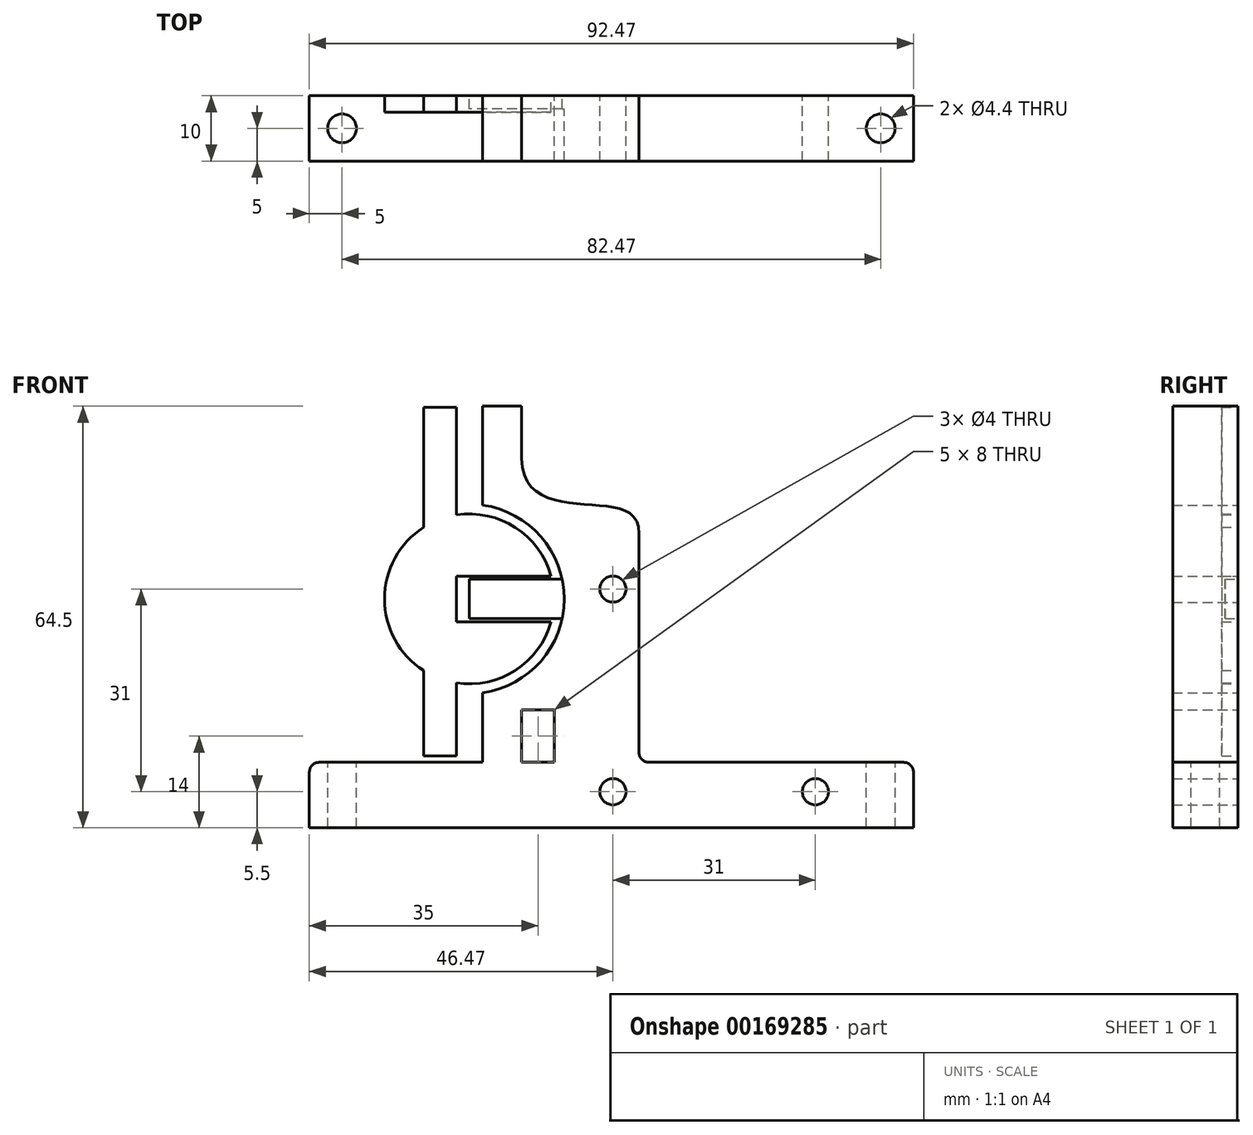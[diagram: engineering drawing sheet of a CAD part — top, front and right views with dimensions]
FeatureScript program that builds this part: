
annotation { "Feature Type Name" : "Feature", "Feature Type Description" : "" }
export const myFeature = defineFeature(function(context is Context, id is Id, definition is map)
    precondition{}
    {
        {
            var Q0;
            Q0=qCreatedBy(makeId("Front.planeOp"),FACE);
            var sketch = newSketch(context, id + "F0", { "sketchPlane" : qUnion([Q0])});
            skLineSegment(sketch, "E0.bottom", {"start": v(0, 0) * mm, "end": v(52, 0) * mm});
            skLineSegment(sketch, "E0.top", {"start": v(0, 10) * mm, "end": v(52, 10) * mm});
            skLineSegment(sketch, "E0.right", {"start": v(52, 0) * mm, "end": v(52, 10) * mm});
            skPoint(sketch, "E1", {"position": v(6, 5.5) * mm});
            skPoint(sketch, "E2", {"position": v(37, 5.5) * mm});
            skLineSegment(sketch, "E3", {"start": v(0, 0) * mm, "end": v(0, 45) * mm, "construction": true});
            skLineSegment(sketch, "E4", {"start": v(0, 45) * mm, "end": v(10, 45) * mm, "construction": true});
            skLineSegment(sketch, "E5", {"start": v(10, 45) * mm, "end": v(10, 10) * mm});
            skLineSegment(sketch, "E6", {"start": v(6, 0) * mm, "end": v(6, 45) * mm, "construction": true});
            skPoint(sketch, "E7", {"position": v(6, 36.5) * mm});
            skLineSegment(sketch, "E8", {"start": v(0, 5.5) * mm, "end": v(52, 5.5) * mm, "construction": true});
            skCircle(sketch, "E9", {"center": v(21.5, 21) * mm, "radius": 21.92 * mm, "construction": true});
            skCircle(sketch, "E10", {"center": v(21.5, 21) * mm, "radius": 10 * mm, "construction": true});
            skCircle(sketch, "E11", {"center": v(21.5, 21) * mm, "radius": 40 * mm, "construction": true});
            skPoint(sketch, "E12", {"position": v(-15.97, 35) * mm});
            skCircle(sketch, "E13", {"center": v(-15.97, 35) * mm, "radius": 11 * mm, "construction": true});
            skCircle(sketch, "E14", {"center": v(-15.97, 35) * mm, "radius": 7.5 * mm, "construction": true});
            skCircle(sketch, "E15", {"center": v(-15.97, 35) * mm, "radius": 14.5 * mm});
            skLineSegment(sketch, "E16", {"start": v(-30.47, 35) * mm, "end": v(-30.47, 0) * mm, "construction": true});
            skLineSegment(sketch, "E17", {"start": v(0, 0) * mm, "end": v(-30.47, 0) * mm});
            skLineSegment(sketch, "E18", {"start": v(-30.47, 0) * mm, "end": v(-40.47, 0) * mm});
            skLineSegment(sketch, "E19", {"start": v(-40.47, 0) * mm, "end": v(-40.47, 10) * mm});
            skLineSegment(sketch, "E20", {"start": v(-40.47, 10) * mm, "end": v(-30.47, 10) * mm});
            skLineSegment(sketch, "E21", {"start": v(21.5, 21) * mm, "end": v(-15.97, 35) * mm, "construction": true});
            skLineSegment(sketch, "E22", {"start": v(-15.97, 68.93) * mm, "end": v(-15.97, 10) * mm, "construction": true});
            skLineSegment(sketch, "E23", {"start": v(-30.47, 10) * mm, "end": v(0, 10) * mm});
            skLineSegment(sketch, "E24", {"start": v(-13.97, 10) * mm, "end": v(-13.97, 64.5) * mm});
            skLineSegment(sketch, "E25", {"start": v(-13.97, 64.5) * mm, "end": v(-7.97, 64.5) * mm});
            skLineSegment(sketch, "E26", {"start": v(-15.97, 38) * mm, "end": v(-15.97, 32) * mm});
            skLineSegment(sketch, "E27", {"start": v(-15.97, 32) * mm, "end": v(0, 32) * mm});
            skLineSegment(sketch, "E28", {"start": v(0, 32) * mm, "end": v(0, 38) * mm});
            skLineSegment(sketch, "E29", {"start": v(0, 38) * mm, "end": v(-15.97, 38) * mm});
            skLineSegment(sketch, "E30", {"start": v(-7.97, 64.5) * mm, "end": v(-7.97, 56.5) * mm});
            skFitSpline(sketch, "E31", {"points": [v(-7.97, 56.5) * mm, v(2.03, 49.43) * mm, v(10, 45) * mm], "startDerivative": vector(0.3, -33.73) * mm, "endDerivative": vector(-0.3, -26.17) * mm});
            skLineSegment(sketch, "E32", {"start": v(-7.97, 10) * mm, "end": v(-7.97, 18) * mm});
            skLineSegment(sketch, "E33", {"start": v(-7.97, 18) * mm, "end": v(-2.97, 18) * mm});
            skLineSegment(sketch, "E34", {"start": v(-2.97, 18) * mm, "end": v(-2.97, 10) * mm});
            skSolve(sketch);
        }
        {
            var Q0;
            {var subQ5=sQuery(id+"F0.wireOp",EDGE,"E0.bottom");Q0=makeQuery(id+"F0.imprint","IMPRINT",FACE,{"disambiguationData":[TD([[makeQuery(id+"F0.imprint","IMPRINT",EDGE,{"derivedFrom":subQ5}),1.0]])]});}
            var Q1;
            {var subQ4=sQuery(id+"F0.wireOp",EDGE,"E4");Q1=makeQuery(id+"F0.imprint","IMPRINT",FACE,{"disambiguationData":[TD([[makeQuery(id+"F0.imprint","IMPRINT",EDGE,{"derivedFrom":subQ4}),-1.0]])]});}
            var Q2;
            {var subQ7=sQuery(id+"F0.wireOp",EDGE,"E17");Q2=makeQuery(id+"F0.imprint","IMPRINT",FACE,{"disambiguationData":[TD([[makeQuery(id+"F0.imprint","IMPRINT",EDGE,{"derivedFrom":subQ7}),-1.0]])]});}
            var Q3;
            {var subQ0=sQuery(id+"F0.wireOp",EDGE,"E18");Q3=makeQuery(id+"F0.imprint","IMPRINT",FACE,{"disambiguationData":[TD([[makeQuery(id+"F0.imprint","IMPRINT",EDGE,{"derivedFrom":subQ0}),-1.0]])]});}
            var Q4;
            Q4=makeQuery(id+"F0.imprint","IMPRINT",FACE,{"disambiguationData":[TD([[makeQuery(id+"F0.imprint","IMPRINT",EDGE,{"derivedFrom":sQuery(id+"F0.wireOp",EDGE,"E4")}),1.0]])]});
            var Q5;
            {var subQ0=sQuery(id+"F0.wireOp",EDGE,"E25");Q5=makeQuery(id+"F0.imprint","IMPRINT",FACE,{"disambiguationData":[TD([[makeQuery(id+"F0.imprint","IMPRINT",EDGE,{"derivedFrom":subQ0}),-1.0]])]});}
            var Q6;
            {var subQ5=sQuery(id+"F0.wireOp",EDGE,"E28");Q6=makeQuery(id+"F0.imprint","IMPRINT",FACE,{"disambiguationData":[TD([[makeQuery(id+"F0.imprint","IMPRINT",EDGE,{"derivedFrom":subQ5}),1.0]])]});}
            var Q7;
            {var subQ0=sQuery(id+"F0.wireOp",EDGE,"E24");var subQ1=sQuery(id+"F0.wireOp",EDGE,"E15");var subQ2=makeQuery(id+"F0.imprint","INTERSECT",VERTEX,{"disambiguationData":[OD(1.0)],"derivedFrom":[subQ1,subQ0]});Q7=makeQuery(id+"F0.imprint","IMPRINT",FACE,{"disambiguationData":[TD([[makeQuery(id+"F0.imprint","IMPRINT",EDGE,{"disambiguationData":[TD([[subQ2,-1.0]])],"derivedFrom":subQ1}),-1.0]])]});}
            extrude(context, id + "F1", {"entities" : qUnion([Q0, Q1, Q2, Q3, Q4, Q5, Q6, Q7]), "depth" : 10 * mm});
        }
        {
            var Q0;
            Q0=sQuery(id+"F0.wireOp",VERTEX,"E7");
            var Q1;
            Q1=sQuery(id+"F0.wireOp",VERTEX,"E1");
            var Q2;
            Q2=sQuery(id+"F0.wireOp",VERTEX,"E2");
            var Q3;
            Q3=makeQuery(id+"F1.opExtrude","SWEPT_BODY",BODY,{"disambiguationData":[OSD([sQuery(id+"F0.wireOp",EDGE,"E0.bottom"),sQuery(id+"F0.wireOp",EDGE,"E0.top"),sQuery(id+"F0.wireOp",EDGE,"E0.right"),sQuery(id+"F0.wireOp",EDGE,"E4"),sQuery(id+"F0.wireOp",EDGE,"E5"),sQuery(id+"F0.wireOp",EDGE,"E15"),sQuery(id+"F0.wireOp",EDGE,"E17"),sQuery(id+"F0.wireOp",EDGE,"E18"),sQuery(id+"F0.wireOp",EDGE,"E19"),sQuery(id+"F0.wireOp",EDGE,"E20"),sQuery(id+"F0.wireOp",EDGE,"Px57lK6U-PPyR-QxDG-lkTx-4ku2XlHoAHPM"),sQuery(id+"F0.wireOp",EDGE,"9lGXsvYk-Ba66-BwJE-tG4q-ajGsNSx14eTR"),sQuery(id+"F0.wireOp",EDGE,"7AF7hhR4-0pg7-JyBW-10Vu-YeYs19Hmrawn"),sQuery(id+"F0.wireOp",EDGE,"SDQQGvJ1-Wn1U-Uzs4-qJnu-05INEi9zJf3w"),sQuery(id+"F0.wireOp",EDGE,"92fyXlvB-mwCe-QFS7-udCC-Qqv6sfzYrIQP"),sQuery(id+"F0.wireOp",EDGE,"BwISZ355-k5cW-KgOS-BZip-VC8WJniyM8gW")])]});
            hole(context, id + "F2", {"style" : HoleStyle.SIMPLE, "endStyle" : HoleEndStyle.THROUGH, "oppositeDirection" : true, "holeDiameter" : 4 * mm, "locations" : qUnion([Q0, Q1, Q2]), "scope" : qUnion([Q3]), "isTappedThrough" : true});
        }
        {
            var Q0;
            {var subQ0=sQuery(id+"F0.wireOp",EDGE,"E29");var subQ1=sQuery(id+"F0.wireOp",EDGE,"E15");var subQ2=makeQuery(id+"F0.imprint","INTERSECT",VERTEX,{"derivedFrom":[subQ1,subQ0]});Q0=makeQuery(id+"F0.imprint","IMPRINT",FACE,{"disambiguationData":[TD([[makeQuery(id+"F0.imprint","IMPRINT",EDGE,{"disambiguationData":[TD([[subQ2,1.0]])],"derivedFrom":subQ1}),1.0]])]});}
            var Q1;
            {var subQ5=sQuery(id+"F0.wireOp",EDGE,"E26");Q1=makeQuery(id+"F0.imprint","IMPRINT",FACE,{"disambiguationData":[TD([[makeQuery(id+"F0.imprint","IMPRINT",EDGE,{"derivedFrom":subQ5}),1.0]])]});}
            extrude(context, id + "F3", {"entities" : qUnion([Q0, Q1]), "operationType" : NewBodyOperationType.ADD, "depth" : 2 * mm});
        }
        {
            var Q0;
            Q0=qCreatedBy(makeId("Front.planeOp"),FACE);
            var sketch = newSketch(context, id + "F4", { "sketchPlane" : qUnion([Q0])});
            skCircle(sketch, "E35", {"center": v(-15.97, 35) * mm, "radius": 13 * mm});
            skLineSegment(sketch, "E36", {"start": v(-3.45, 38.5) * mm, "end": v(-17.97, 38.5) * mm});
            skLineSegment(sketch, "E37", {"start": v(-17.97, 38.5) * mm, "end": v(-17.97, 31.5) * mm});
            skLineSegment(sketch, "E38", {"start": v(-17.97, 31.5) * mm, "end": v(-3.45, 31.5) * mm});
            skLineSegment(sketch, "E39", {"start": v(-15.97, 35) * mm, "end": v(-15.97, 70.7) * mm, "construction": true});
            skLineSegment(sketch, "E40", {"start": v(-17.97, 47.85) * mm, "end": v(-17.97, 64.35) * mm});
            skLineSegment(sketch, "E41", {"start": v(-17.97, 64.35) * mm, "end": v(-22.97, 64.35) * mm});
            skLineSegment(sketch, "E42", {"start": v(-22.97, 64.35) * mm, "end": v(-22.97, 45.95) * mm});
            skLineSegment(sketch, "E43", {"start": v(-17.97, 22.15) * mm, "end": v(-17.97, 11) * mm});
            skLineSegment(sketch, "E44", {"start": v(-17.97, 11) * mm, "end": v(-22.97, 11) * mm});
            skLineSegment(sketch, "E45", {"start": v(-22.97, 11) * mm, "end": v(-22.97, 24.05) * mm});
            skSolve(sketch);
        }
        {
            var Q0;
            {var subQ6=sQuery(id+"F4.wireOp",EDGE,"E36");Q0=makeQuery(id+"F4.imprint","IMPRINT",FACE,{"disambiguationData":[TD([[makeQuery(id+"F4.imprint","IMPRINT",EDGE,{"derivedFrom":subQ6}),-1.0]])]});}
            var Q1;
            {var subQ0=sQuery(id+"F4.wireOp",EDGE,"E40");Q1=makeQuery(id+"F4.imprint","IMPRINT",FACE,{"disambiguationData":[TD([[makeQuery(id+"F4.imprint","IMPRINT",EDGE,{"derivedFrom":subQ0}),1.0]])]});}
            var Q2;
            {var subQ0=sQuery(id+"F4.wireOp",EDGE,"E43");Q2=makeQuery(id+"F4.imprint","IMPRINT",FACE,{"disambiguationData":[TD([[makeQuery(id+"F4.imprint","IMPRINT",EDGE,{"derivedFrom":subQ0}),-1.0]])]});}
            extrude(context, id + "F5", {"entities" : qUnion([Q0, Q1, Q2]), "depth" : 2.5 * mm});
        }
        {
            var Q0;
            Q0=makeQuery(id+"F1.opExtrude","SWEPT_FACE",FACE,{"disambiguationData":[OSD([sQuery(id+"F0.wireOp",EDGE,"E0.top")])]});
            var sketch = newSketch(context, id + "F6", { "sketchPlane" : qUnion([Q0])});
            skPoint(sketch, "E46", {"position": v(47, -5) * mm});
            skPoint(sketch, "E47", {"position": v(-35.47, -5) * mm});
            skSolve(sketch);
        }
        {
            var Q0;
            Q0=sQuery(id+"F6.wireOp",VERTEX,"E46");
            var Q1;
            Q1=sQuery(id+"F6.wireOp",VERTEX,"E47");
            var Q2;
            Q2=makeQuery(id+"F1.opExtrude","SWEPT_BODY",BODY,{"disambiguationData":[OSD([sQuery(id+"F0.wireOp",EDGE,"E0.bottom"),sQuery(id+"F0.wireOp",EDGE,"E0.top"),sQuery(id+"F0.wireOp",EDGE,"E0.right"),sQuery(id+"F0.wireOp",EDGE,"E4"),sQuery(id+"F0.wireOp",EDGE,"E5"),sQuery(id+"F0.wireOp",EDGE,"E14"),sQuery(id+"F0.wireOp",EDGE,"E15"),sQuery(id+"F0.wireOp",EDGE,"E16"),sQuery(id+"F0.wireOp",EDGE,"E17"),sQuery(id+"F0.wireOp",EDGE,"OzwFwTIN-bC5G-Ygy7-q12Z-rKeMtg9WZtUH")])]});
            hole(context, id + "F7", {"style" : HoleStyle.SIMPLE, "endStyle" : HoleEndStyle.THROUGH, "standardTappedOrClearance" : lookupTablePath({ "standard" : "ISO", "fit" : "Normal", "size" : "M4", "type" : "Clearance" }), "standardBlindInLast" : lookupTablePath({ "fit" : "Standard", "standard" : "ISO", "size" : "M4", "type" : "Clearance" }), "holeDiameter" : 4.4 * mm, "locations" : qUnion([Q0, Q1]), "scope" : qUnion([Q2]), "isTappedThrough" : true});
        }
        {
            var Q0;
            Q0=makeQuery(id+"F1.opExtrude","SWEPT_EDGE",EDGE,{"disambiguationData":[OSD([sQuery(id+"F0.wireOp",EDGE,"E19"),sQuery(id+"F0.wireOp",EDGE,"E20")])]});
            var Q1;
            Q1=makeQuery(id+"F1.opExtrude","SWEPT_EDGE",EDGE,{"disambiguationData":[OSD([sQuery(id+"F0.wireOp",EDGE,"E16"),sQuery(id+"F0.wireOp",EDGE,"E20")])]});
            var Q2;
            Q2=makeQuery(id+"F1.opExtrude","SWEPT_EDGE",EDGE,{"disambiguationData":[OSD([sQuery(id+"F0.wireOp",EDGE,"E4"),sQuery(id+"F0.wireOp",EDGE,"E5")])]});
            var Q3;
            Q3=makeQuery(id+"F1.opExtrude","SWEPT_EDGE",EDGE,{"disambiguationData":[OSD([sQuery(id+"F0.wireOp",EDGE,"E0.top"),sQuery(id+"F0.wireOp",EDGE,"E5")])]});
            var Q4;
            Q4=makeQuery(id+"F1.opExtrude","SWEPT_EDGE",EDGE,{"disambiguationData":[OSD([sQuery(id+"F0.wireOp",EDGE,"E0.top"),sQuery(id+"F0.wireOp",EDGE,"E0.right")])]});
            fillet(context, id + "F8", {"entities" : qUnion([Q0, Q1, Q2, Q3, Q4]), "radius" : 1.5 * mm, "tangentPropagation" : true, "allowEdgeOverflow" : false});
        }
    });
